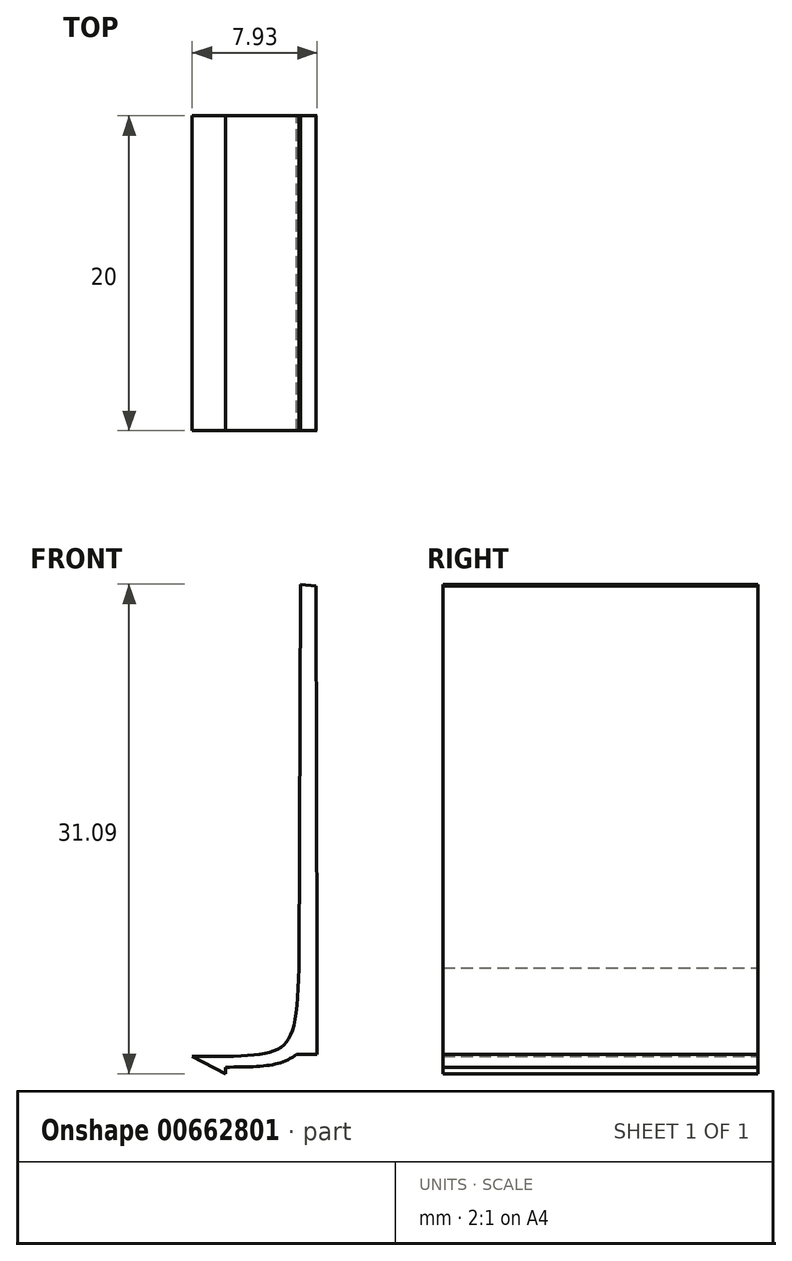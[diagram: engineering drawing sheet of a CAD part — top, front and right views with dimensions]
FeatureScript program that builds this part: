
annotation { "Feature Type Name" : "Feature", "Feature Type Description" : "" }
export const myFeature = defineFeature(function(context is Context, id is Id, definition is map)
    precondition{}
    {
        {
            var Q0;
            Q0=qCreatedBy(makeId("Front.planeOp"),FACE);
            var sketch = newSketch(context, id + "F0", { "sketchPlane" : qUnion([Q0])});
            skLineSegment(sketch, "E0.MirrorCS", {"start": v(4.67, 4.29) * mm, "end": v(5.82, 4.29) * mm});
            skLineSegment(sketch, "E1.MirrorCS", {"start": v(4.78, 28.66) * mm, "end": v(5.74, 28.56) * mm});
            skLineSegment(sketch, "E2.MirrorCS", {"start": v(4.67, 4.29) * mm, "end": v(4.78, 28.66) * mm});
            skLineSegment(sketch, "E3.MirrorCS", {"start": v(5.82, 4.29) * mm, "end": v(5.74, 28.56) * mm});
            skFitSpline(sketch, "E4", {"points": [v(5.82, 4.29) * mm, v(0, -2.02) * mm], "startDerivative": vector(-0.05, -18.78) * mm, "endDerivative": vector(-12.7, -0.04) * mm});
            skFitSpline(sketch, "E5", {"points": [v(4.67, 4.29) * mm, v(0, -1.34) * mm], "startDerivative": vector(-0.55, -16.46) * mm, "endDerivative": vector(-12.2, -0.55) * mm});
            skLineSegment(sketch, "E6", {"start": v(0, -1.34) * mm, "end": v(0, -2.02) * mm});
            skLineSegment(sketch, "E7", {"start": v(0, -2.02) * mm, "end": v(0, -2.43) * mm});
            skLineSegment(sketch, "E8", {"start": v(0, -1.34) * mm, "end": v(-2.11, -1.34) * mm});
            skLineSegment(sketch, "E9", {"start": v(-2.11, -1.34) * mm, "end": v(0, -2.43) * mm});
            skLineSegment(sketch, "E10", {"start": v(5.82, 4.29) * mm, "end": v(5.8, -1.2) * mm});
            skLineSegment(sketch, "E11", {"start": v(5.8, -1.2) * mm, "end": v(4.49, -1.2) * mm});
            skLineSegment(sketch, "E12", {"start": v(4.67, 4.29) * mm, "end": v(4.49, -1.2) * mm});
            skSolve(sketch);
        }
        {
            var Q0;
            Q0=qSketchRegion(id+"F0",true);
            extrude(context, id + "F1", {"entities" : qUnion([Q0]), "depth" : 20 * mm, "offsetDistance" : 25 * mm});
        }
    });
